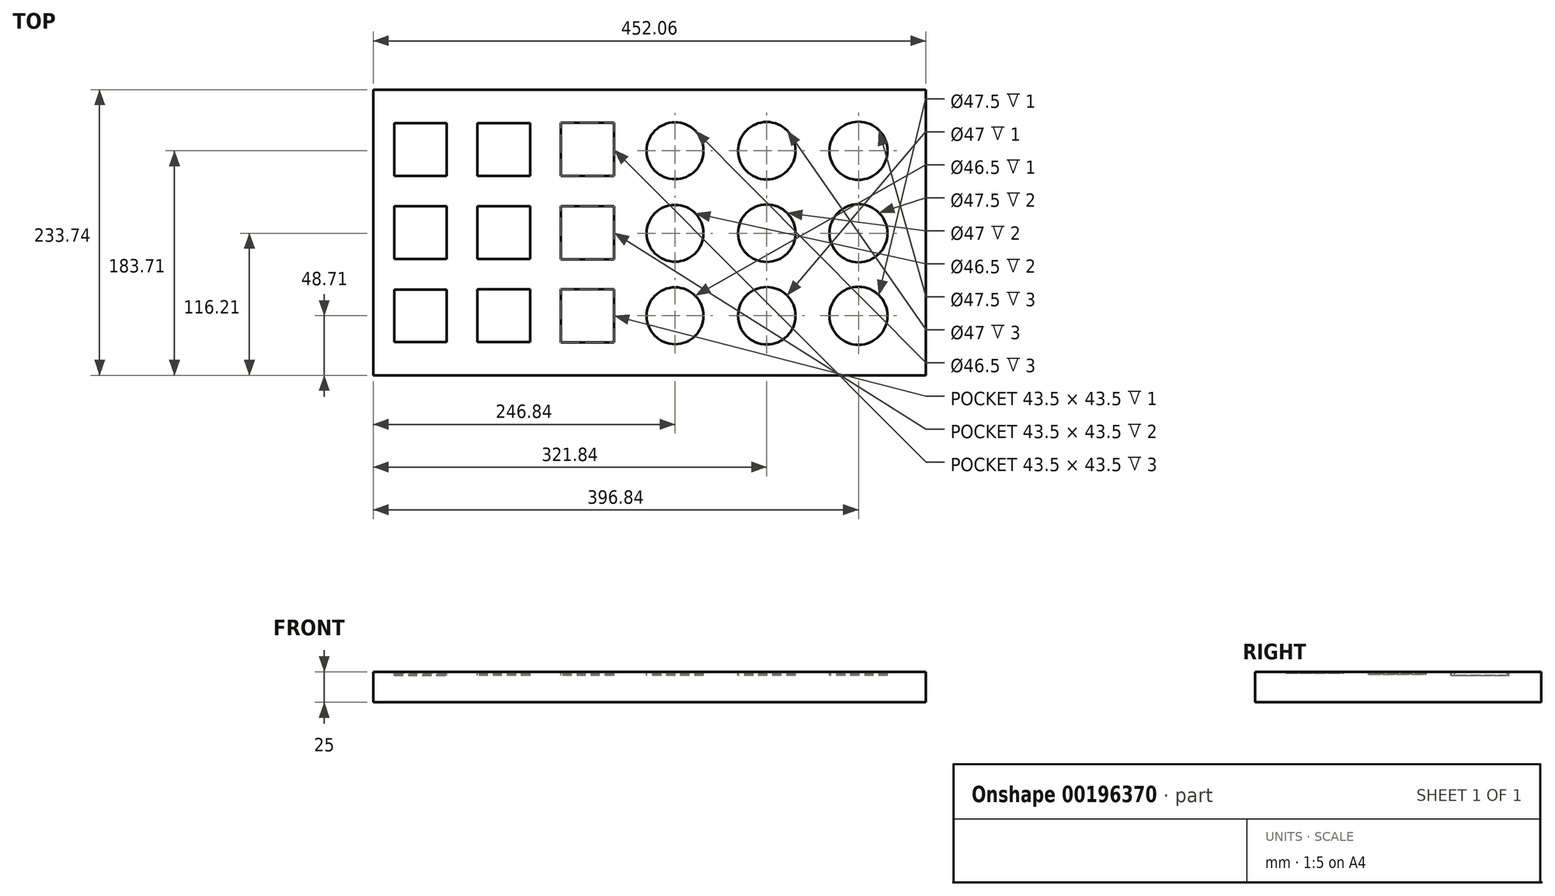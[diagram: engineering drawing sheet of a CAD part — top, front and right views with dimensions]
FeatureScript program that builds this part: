
annotation { "Feature Type Name" : "Feature", "Feature Type Description" : "" }
export const myFeature = defineFeature(function(context is Context, id is Id, definition is map)
    precondition{}
    {
        {
            var Q0;
            Q0=qCreatedBy(makeId("Top.planeOp"),FACE);
            var sketch = newSketch(context, id + "F0", { "sketchPlane" : qUnion([Q0])});
            skLineSegment(sketch, "E0", {"start": v(0, 0) * mm, "end": v(157.3, 0) * mm, "construction": true});
            skLineSegment(sketch, "E1.bottom", {"start": v(21.5, -21.5) * mm, "end": v(-21.5, -21.5) * mm});
            skLineSegment(sketch, "E1.top", {"start": v(21.5, 21.5) * mm, "end": v(-21.5, 21.5) * mm});
            skLineSegment(sketch, "E1.left", {"start": v(21.5, -21.5) * mm, "end": v(21.5, 21.5) * mm});
            skLineSegment(sketch, "E1.right", {"start": v(-21.5, -21.5) * mm, "end": v(-21.5, 21.5) * mm});
            skPoint(sketch, "E1.middle", {"position": v(0, 0) * mm});
            skLineSegment(sketch, "E2.bottom", {"start": v(89.75, -21.63) * mm, "end": v(46.5, -21.63) * mm});
            skLineSegment(sketch, "E2.top", {"start": v(89.75, 21.62) * mm, "end": v(46.5, 21.62) * mm});
            skLineSegment(sketch, "E2.left", {"start": v(89.75, -21.63) * mm, "end": v(89.75, 21.62) * mm});
            skLineSegment(sketch, "E2.right", {"start": v(46.5, -21.63) * mm, "end": v(46.5, 21.62) * mm});
            skPoint(sketch, "E2.middle", {"position": v(68.12, 0) * mm});
            skLineSegment(sketch, "E3.bottom", {"start": v(158.25, 21.75) * mm, "end": v(114.75, 21.75) * mm});
            skLineSegment(sketch, "E3.top", {"start": v(158.25, -21.75) * mm, "end": v(114.75, -21.75) * mm});
            skLineSegment(sketch, "E3.left", {"start": v(158.25, 21.75) * mm, "end": v(158.25, -21.75) * mm});
            skLineSegment(sketch, "E3.right", {"start": v(114.75, 21.75) * mm, "end": v(114.75, -21.75) * mm});
            skPoint(sketch, "E3.middle", {"position": v(136.5, 0) * mm});
            skSolve(sketch);
        }
        {
            var Q0;
            Q0=qCreatedBy(makeId("Top.planeOp"),FACE);
            var sketch = newSketch(context, id + "F1", { "sketchPlane" : qUnion([Q0])});
            skLineSegment(sketch, "E4", {"start": v(0, 0) * mm, "end": v(0, 136) * mm, "construction": true});
            skLineSegment(sketch, "E5", {"start": v(0, 68) * mm, "end": v(205.63, 68) * mm, "construction": true});
            skLineSegment(sketch, "E6.bottom", {"start": v(-21.5, 46.5) * mm, "end": v(21.5, 46.5) * mm});
            skLineSegment(sketch, "E6.top", {"start": v(-21.5, 89.5) * mm, "end": v(21.5, 89.5) * mm});
            skLineSegment(sketch, "E6.left", {"start": v(-21.5, 46.5) * mm, "end": v(-21.5, 89.5) * mm});
            skLineSegment(sketch, "E6.right", {"start": v(21.5, 46.5) * mm, "end": v(21.5, 89.5) * mm});
            skPoint(sketch, "E6.middle", {"position": v(0, 68) * mm});
            skLineSegment(sketch, "E7.bottom", {"start": v(89.75, 89.62) * mm, "end": v(46.5, 89.62) * mm});
            skLineSegment(sketch, "E7.top", {"start": v(89.75, 46.37) * mm, "end": v(46.5, 46.37) * mm});
            skLineSegment(sketch, "E7.left", {"start": v(89.75, 89.62) * mm, "end": v(89.75, 46.38) * mm});
            skLineSegment(sketch, "E7.right", {"start": v(46.5, 89.62) * mm, "end": v(46.5, 46.37) * mm});
            skPoint(sketch, "E7.middle", {"position": v(68.12, 68) * mm});
            skLineSegment(sketch, "E8.bottom", {"start": v(158.25, 89.75) * mm, "end": v(114.75, 89.75) * mm});
            skLineSegment(sketch, "E8.top", {"start": v(158.25, 46.25) * mm, "end": v(114.75, 46.25) * mm});
            skLineSegment(sketch, "E8.left", {"start": v(158.25, 89.75) * mm, "end": v(158.25, 46.25) * mm});
            skLineSegment(sketch, "E8.right", {"start": v(114.75, 89.75) * mm, "end": v(114.75, 46.25) * mm});
            skPoint(sketch, "E8.middle", {"position": v(136.5, 68) * mm});
            skSolve(sketch);
        }
        {
            var Q0;
            Q0=qCreatedBy(makeId("Top.planeOp"),FACE);
            var sketch = newSketch(context, id + "F2", { "sketchPlane" : qUnion([Q0])});
            skLineSegment(sketch, "E9", {"start": v(0, 136) * mm, "end": v(186.8, 136) * mm, "construction": true});
            skLineSegment(sketch, "E10.bottom", {"start": v(-21.5, 114.5) * mm, "end": v(21.5, 114.5) * mm});
            skLineSegment(sketch, "E10.top", {"start": v(-21.5, 157.5) * mm, "end": v(21.5, 157.5) * mm});
            skLineSegment(sketch, "E10.left", {"start": v(-21.5, 114.5) * mm, "end": v(-21.5, 157.5) * mm});
            skLineSegment(sketch, "E10.right", {"start": v(21.5, 114.5) * mm, "end": v(21.5, 157.5) * mm});
            skPoint(sketch, "E10.middle", {"position": v(0, 136) * mm});
            skLineSegment(sketch, "E11.bottom", {"start": v(89.75, 157.62) * mm, "end": v(46.5, 157.62) * mm});
            skLineSegment(sketch, "E11.top", {"start": v(89.75, 114.37) * mm, "end": v(46.5, 114.37) * mm});
            skLineSegment(sketch, "E11.left", {"start": v(89.75, 157.62) * mm, "end": v(89.75, 114.37) * mm});
            skLineSegment(sketch, "E11.right", {"start": v(46.5, 157.62) * mm, "end": v(46.5, 114.37) * mm});
            skPoint(sketch, "E11.middle", {"position": v(68.12, 136) * mm});
            skLineSegment(sketch, "E12.bottom", {"start": v(158.25, 157.75) * mm, "end": v(114.75, 157.75) * mm});
            skLineSegment(sketch, "E12.top", {"start": v(158.25, 114.25) * mm, "end": v(114.75, 114.25) * mm});
            skLineSegment(sketch, "E12.left", {"start": v(158.25, 157.75) * mm, "end": v(158.25, 114.25) * mm});
            skLineSegment(sketch, "E12.right", {"start": v(114.75, 157.75) * mm, "end": v(114.75, 114.25) * mm});
            skPoint(sketch, "E12.middle", {"position": v(136.5, 136) * mm});
            skSolve(sketch);
        }
        {
            var Q0;
            Q0=qCreatedBy(makeId("Top.planeOp"),FACE);
            var sketch = newSketch(context, id + "F3", { "sketchPlane" : qUnion([Q0])});
            skLineSegment(sketch, "E13.bottom", {"start": v(-38.6, -48.71) * mm, "end": v(413.47, -48.71) * mm});
            skLineSegment(sketch, "E13.top", {"start": v(-38.6, 185.03) * mm, "end": v(413.47, 185.03) * mm});
            skLineSegment(sketch, "E13.left", {"start": v(-38.6, -48.71) * mm, "end": v(-38.6, 185.03) * mm});
            skLineSegment(sketch, "E13.right", {"start": v(413.47, -48.71) * mm, "end": v(413.47, 185.03) * mm});
            skSolve(sketch);
        }
        {
            var Q0;
            Q0 = qSketchRegion(id + "F3", true);
            extrude(context, id + "F4", {"entities" : qUnion([Q0]), "oppositeDirection" : true, "depth" : 25 * mm});
        }
        {
            var Q0;
            Q0 = qSketchRegion(id + "F0", true);
            extrude(context, id + "F5", {"entities" : qUnion([Q0]), "operationType" : NewBodyOperationType.REMOVE, "oppositeDirection" : true, "depth" : 1 * mm});
        }
        {
            var Q0;
            Q0 = qSketchRegion(id + "F1", true);
            extrude(context, id + "F6", {"entities" : qUnion([Q0]), "operationType" : NewBodyOperationType.REMOVE, "oppositeDirection" : true, "depth" : 2 * mm});
        }
        {
            var Q0;
            Q0 = qSketchRegion(id + "F2", true);
            extrude(context, id + "F7", {"entities" : qUnion([Q0]), "operationType" : NewBodyOperationType.REMOVE, "oppositeDirection" : true, "depth" : 3 * mm});
        }
        {
            var Q0;
            Q0=makeQuery(id+"F4.opExtrude","CAP_FACE",FACE,{"disambiguationData":[OSD([sQuery(id+"F3.wireOp",EDGE,"E13.bottom"),sQuery(id+"F3.wireOp",EDGE,"E13.top"),sQuery(id+"F3.wireOp",EDGE,"E13.left"),sQuery(id+"F3.wireOp",EDGE,"E13.right")])],"isStart":true});
            var sketch = newSketch(context, id + "F8", { "sketchPlane" : qUnion([Q0])});
            skLineSegment(sketch, "E14", {"start": v(0, 0) * mm, "end": v(450.99, 0) * mm, "construction": true});
            skPoint(sketch, "E14.endSnap0", {"position": v(158.25, 0) * mm});
            skCircle(sketch, "E15", {"center": v(208.25, 0) * mm, "radius": 23.25 * mm});
            skCircle(sketch, "E16", {"center": v(283.25, 0) * mm, "radius": 23.5 * mm});
            skCircle(sketch, "E17", {"center": v(358.25, 0) * mm, "radius": 23.75 * mm});
            skSolve(sketch);
        }
        {
            var Q0;
            Q0=makeQuery(id+"F8.imprint","IMPRINT",FACE,{"disambiguationData":[TD([[makeQuery(id+"F8.imprint","IMPRINT",EDGE,{"derivedFrom":sQuery(id+"F8.wireOp",EDGE,"E15")}),-1.0]])]});
            var sketch = newSketch(context, id + "F9", { "sketchPlane" : qUnion([Q0])});
            skLineSegment(sketch, "E18", {"start": v(0, 0) * mm, "end": v(0, 176.5) * mm, "construction": true});
            skLineSegment(sketch, "E19", {"start": v(0, 67.5) * mm, "end": v(381.78, 67.5) * mm, "construction": true});
            skCircle(sketch, "E20", {"center": v(208.25, 67.5) * mm, "radius": 23.25 * mm});
            skCircle(sketch, "E21", {"center": v(283.25, 67.5) * mm, "radius": 23.5 * mm});
            skCircle(sketch, "E22", {"center": v(358.25, 67.5) * mm, "radius": 23.75 * mm});
            skLineSegment(sketch, "E23", {"start": v(0, 135) * mm, "end": v(382.93, 135) * mm, "construction": true});
            skSolve(sketch);
        }
        {
            var Q0;
            Q0=makeQuery(id+"F8.imprint","IMPRINT",FACE,{"disambiguationData":[TD([[makeQuery(id+"F8.imprint","IMPRINT",EDGE,{"derivedFrom":sQuery(id+"F8.wireOp",EDGE,"E15")}),-1.0]])]});
            var sketch = newSketch(context, id + "F10", { "sketchPlane" : qUnion([Q0])});
            skLineSegment(sketch, "E24", {"start": v(0, 0) * mm, "end": v(0, 175.46) * mm, "construction": true});
            skLineSegment(sketch, "E25", {"start": v(0, 135) * mm, "end": v(416.5, 135) * mm, "construction": true});
            skCircle(sketch, "E26", {"center": v(208.25, 135) * mm, "radius": 23.25 * mm});
            skCircle(sketch, "E27", {"center": v(283.25, 135) * mm, "radius": 23.5 * mm});
            skCircle(sketch, "E28", {"center": v(358.25, 135) * mm, "radius": 23.75 * mm});
            skSolve(sketch);
        }
        {
            var Q0;
            Q0 = qSketchRegion(id + "F8", true);
            extrude(context, id + "F11", {"entities" : qUnion([Q0]), "operationType" : NewBodyOperationType.REMOVE, "oppositeDirection" : true, "depth" : 1 * mm});
        }
        {
            var Q0;
            Q0 = qSketchRegion(id + "F9", true);
            extrude(context, id + "F12", {"entities" : qUnion([Q0]), "operationType" : NewBodyOperationType.REMOVE, "oppositeDirection" : true, "depth" : 2 * mm});
        }
        {
            var Q0;
            Q0 = qSketchRegion(id + "F10", true);
            extrude(context, id + "F13", {"entities" : qUnion([Q0]), "operationType" : NewBodyOperationType.REMOVE, "oppositeDirection" : true, "depth" : 3 * mm});
        }
    });
